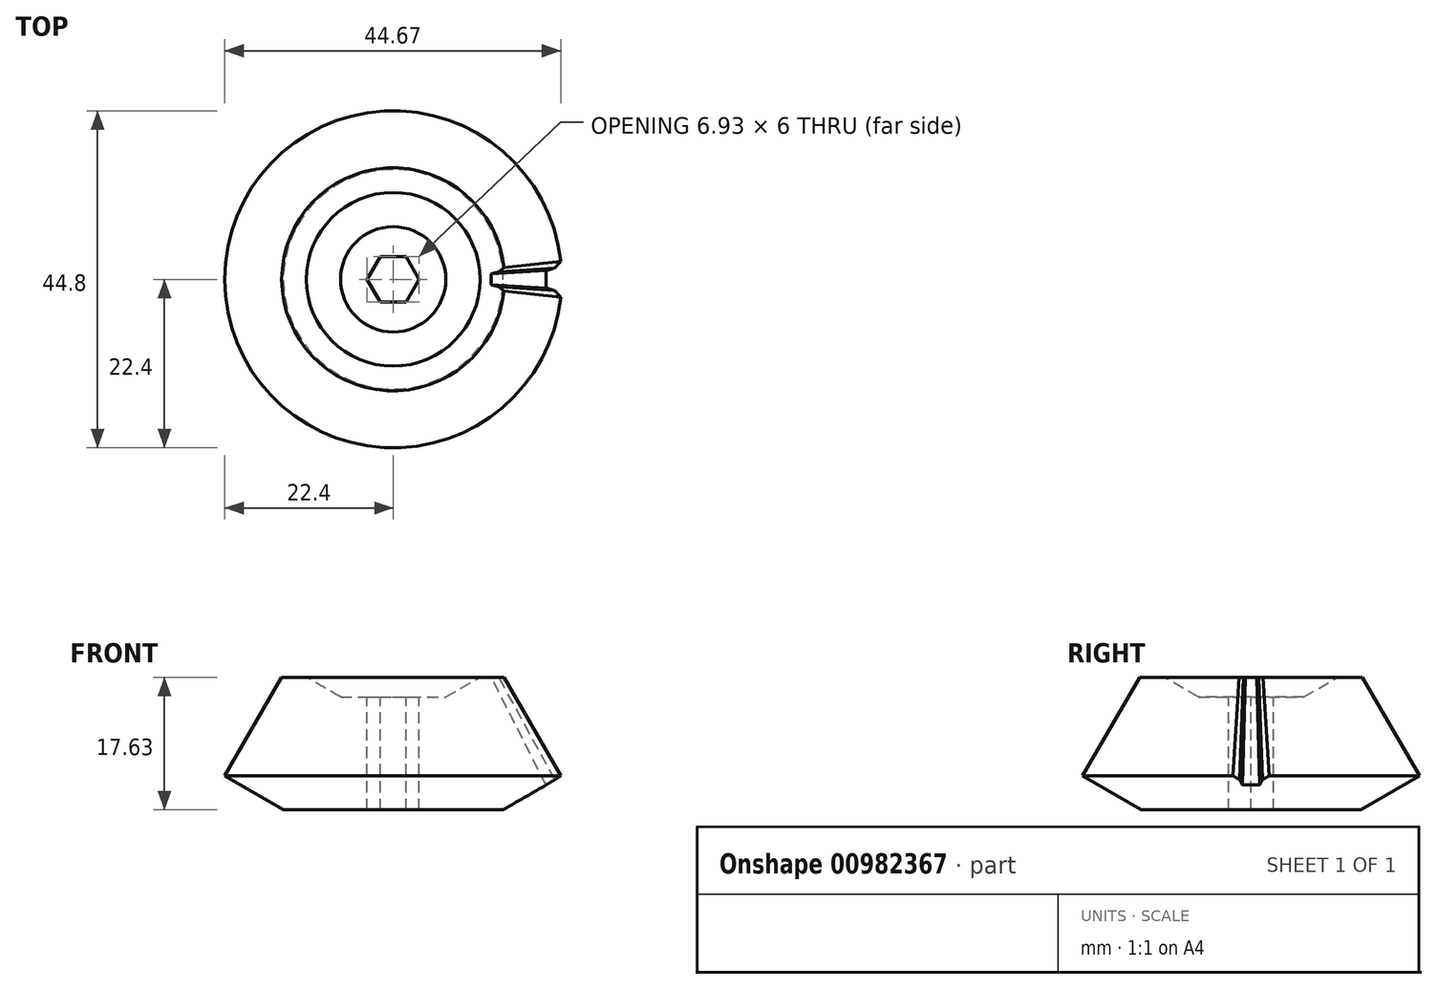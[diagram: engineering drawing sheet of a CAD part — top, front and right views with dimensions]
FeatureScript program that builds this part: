
annotation { "Feature Type Name" : "Feature", "Feature Type Description" : "" }
export const myFeature = defineFeature(function(context is Context, id is Id, definition is map)
    precondition{}
    {
        {
            var Q0;
            Q0=qCreatedBy(makeId("Front.planeOp"),FACE);
            var sketch = newSketch(context, id + "F0", { "sketchPlane" : qUnion([Q0])});
            skLineSegment(sketch, "E0", {"start": v(22.4, 4.5) * mm, "end": v(0, 43.3) * mm});
            skLineSegment(sketch, "E1", {"start": v(0, 43.3) * mm, "end": v(0, 0) * mm});
            skLineSegment(sketch, "E2", {"start": v(0, 0) * mm, "end": v(14.6, 0) * mm});
            skLineSegment(sketch, "E3", {"start": v(14.6, 0) * mm, "end": v(22.4, 4.5) * mm});
            skLineSegment(sketch, "E4", {"start": v(22.4, 4.5) * mm, "end": v(25, 0) * mm});
            skSolve(sketch);
        }
        {
            var Q0;
            Q0=makeQuery(id+"F0.imprint","IMPRINT",FACE,{"disambiguationData":[TD([[makeQuery(id+"F0.imprint","IMPRINT",EDGE,{"derivedFrom":sQuery(id+"F0.wireOp",EDGE,"iZfwdum0-eERQ-opZv-YKFB-7AKXDabp0p0H")}),1.0]])]});
            var Q1;
            Q1=makeQuery(id+"F0.imprint","IMPRINT",FACE,{"disambiguationData":[TD([[makeQuery(id+"F0.imprint","IMPRINT",EDGE,{"derivedFrom":sQuery(id+"F0.wireOp",EDGE,"E0")}),1.0]])]});
            var Q2;
            Q2=sQuery(id+"F0.wireOp",EDGE,"E1");
            revolve(context, id + "F1", {"surfaceOperationType" : NewSurfaceOperationType.NEW, "entities" : qUnion([Q0, Q1]), "axis" : qUnion([Q2]), "revolveType" : RevolveType.FULL});
        }
        {
            var Q0;
            Q0=sQuery(id+"F0.wireOp",EDGE,"E0");
            var Q1;
            Q1=sQuery(id+"F0.wireOp",VERTEX,"E0.start");
            cPlane(context, id + "F2", {"entities" : qUnion([Q0, Q1]), "cplaneType" : CPlaneType.LINE_POINT, "offset" : 25 * mm, "width" : 150 * mm, "height" : 150 * mm});
        }
        {
            var Q0;
            Q0=qCreatedBy(id+"F2.planeOp",FACE);
            var sketch = newSketch(context, id + "F3", { "sketchPlane" : qUnion([Q0])});
            skLineSegment(sketch, "E5", {"start": v(21.65, -2.5) * mm, "end": v(21.65, 2.5) * mm});
            skLineSegment(sketch, "E6", {"start": v(21.65, 0) * mm, "end": v(19.25, 0) * mm, "construction": true});
            skLineSegment(sketch, "E7", {"start": v(19.25, 0) * mm, "end": v(19.25, 1.15) * mm});
            skLineSegment(sketch, "E8", {"start": v(0, 0) * mm, "end": v(21.65, 2.5) * mm, "construction": true});
            skLineSegment(sketch, "E9.MirrorCS", {"start": v(19.25, 0) * mm, "end": v(19.25, -1.15) * mm});
            skLineSegment(sketch, "E10", {"start": v(19.25, 1.15) * mm, "end": v(20.62, 1.52) * mm});
            skLineSegment(sketch, "E11", {"start": v(20.62, 1.52) * mm, "end": v(21.65, 2.5) * mm});
            skLineSegment(sketch, "E12", {"start": v(19.25, 1.15) * mm, "end": v(21.65, 2.5) * mm, "construction": true});
            skLineSegment(sketch, "E13", {"start": v(20.62, 1.52) * mm, "end": v(20.45, 1.83) * mm, "construction": true});
            skLineSegment(sketch, "E14.MirrorCS", {"start": v(19.25, -1.15) * mm, "end": v(20.62, -1.52) * mm});
            skLineSegment(sketch, "E15.MirrorCS", {"start": v(20.62, -1.52) * mm, "end": v(21.65, -2.5) * mm});
            skSolve(sketch);
        }
        {
            var Q0;
            Q0=makeQuery(id+"F3.imprint","IMPRINT",FACE,{"disambiguationData":[TD([[makeQuery(id+"F3.imprint","IMPRINT",EDGE,{"derivedFrom":sQuery(id+"F3.wireOp",EDGE,"E5")}),1.0]])]});
            var Q1;
            Q1=sQuery(id+"F0.wireOp",VERTEX,"E0.end");
            loft(context, id + "F4", {"operationType" : NewBodyOperationType.REMOVE, "sheetProfilesArray" : [{ "sheetProfileEntities" : qUnion([Q0]) }, { "sheetProfileEntities" : qUnion([Q1]) }]});
        }
        {
            var Q0;
            Q0=qCreatedBy(makeId("Front.planeOp"),FACE);
            var sketch = newSketch(context, id + "F5", { "sketchPlane" : qUnion([Q0])});
            skLineSegment(sketch, "E16", {"start": v(0, 0) * mm, "end": v(0, 15) * mm});
            skLineSegment(sketch, "E17", {"start": v(0, 15) * mm, "end": v(7, 15) * mm});
            skLineSegment(sketch, "E18", {"start": v(7, 15) * mm, "end": v(11.55, 17.62) * mm});
            skLineSegment(sketch, "E19", {"start": v(11.55, 17.62) * mm, "end": v(17.55, 17.62) * mm});
            skLineSegment(sketch, "E20", {"start": v(17.55, 17.62) * mm, "end": v(0, 46.75) * mm});
            skLineSegment(sketch, "E21", {"start": v(0, 46.75) * mm, "end": v(0, 15) * mm});
            skSolve(sketch);
        }
        {
            var Q0;
            Q0 = qSketchRegion(id + "F5", true);
            var Q1;
            Q1=sQuery(id+"F5.wireOp",EDGE,"E21");
            revolve(context, id + "F6", {"operationType" : NewBodyOperationType.REMOVE, "surfaceOperationType" : NewSurfaceOperationType.NEW, "entities" : qUnion([Q0]), "axis" : qUnion([Q1]), "revolveType" : RevolveType.FULL, "oppositeDirection" : true});
        }
        {
            var Q0;
            Q0=makeQuery(id+"F6.boolean.opBoolean","COPY",FACE,{"derivedFrom":makeQuery(id+"F6.opRevolve","SWEPT_FACE",FACE,{"disambiguationData":[OSD([sQuery(id+"F5.wireOp",EDGE,"E17")])]})});
            var sketch = newSketch(context, id + "F7", { "sketchPlane" : qUnion([Q0])});
            skCircle(sketch, "E22.cCircle", {"center": v(0, 0) * mm, "radius": 3 * mm, "construction": true});
            skLineSegment(sketch, "E22.0", {"start": v(-1.73, 3) * mm, "end": v(1.73, 3) * mm});
            skLineSegment(sketch, "E22.1", {"start": v(1.73, 3) * mm, "end": v(3.46, 0) * mm});
            skLineSegment(sketch, "E22.2", {"start": v(3.46, 0) * mm, "end": v(1.73, -3) * mm});
            skLineSegment(sketch, "E22.3", {"start": v(1.73, -3) * mm, "end": v(-1.73, -3) * mm});
            skLineSegment(sketch, "E22.4", {"start": v(-1.73, -3) * mm, "end": v(-3.46, 0) * mm});
            skLineSegment(sketch, "E22.5", {"start": v(-3.46, 0) * mm, "end": v(-1.73, 3) * mm});
            skPoint(sketch, "E22.0.midPoint", {"position": v(0, 3) * mm});
            skSolve(sketch);
        }
        {
            var Q0;
            Q0 = qSketchRegion(id + "F7", true);
            extrude(context, id + "F8", {"entities" : qUnion([Q0]), "operationType" : NewBodyOperationType.REMOVE, "endBound" : BoundingType.THROUGH_ALL, "oppositeDirection" : true, "depth" : 25 * mm, "offsetDistance" : 25 * mm});
        }
    });
